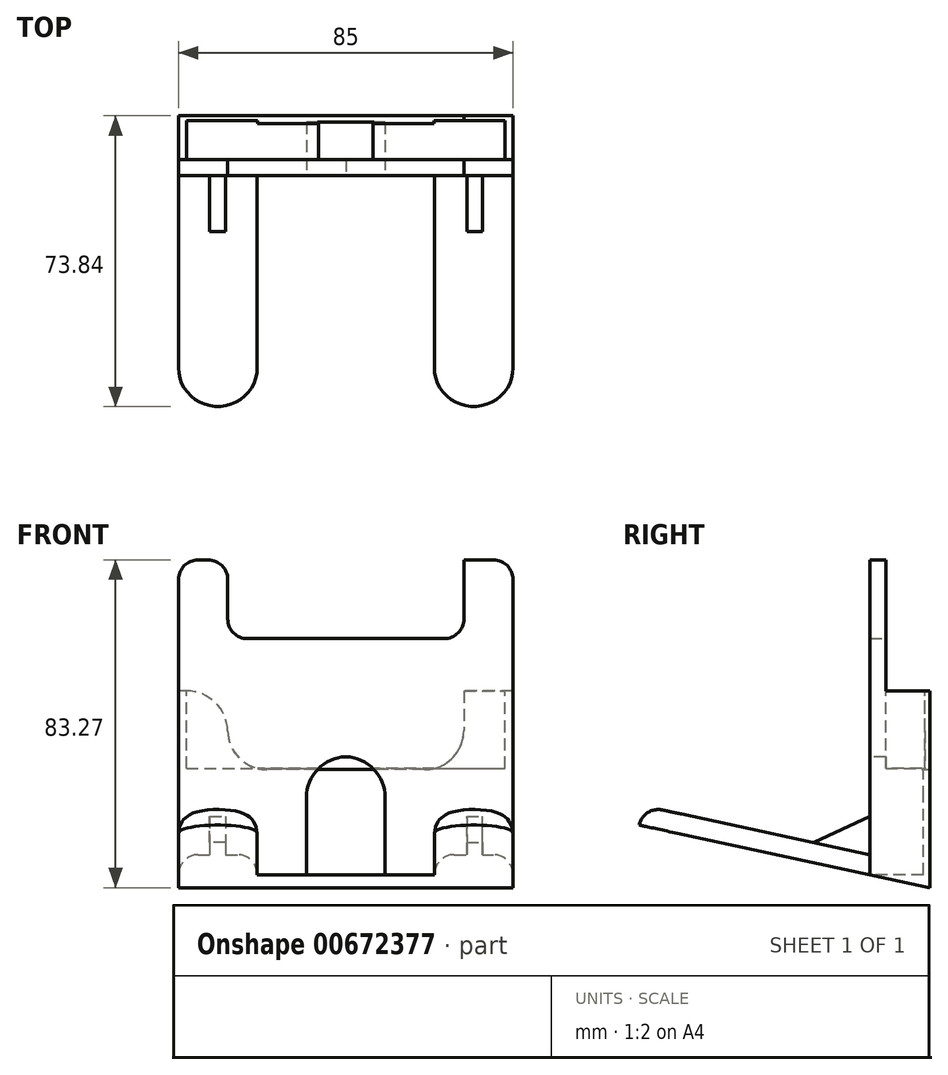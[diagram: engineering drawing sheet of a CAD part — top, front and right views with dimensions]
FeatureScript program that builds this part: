
annotation { "Feature Type Name" : "Feature", "Feature Type Description" : "" }
export const myFeature = defineFeature(function(context is Context, id is Id, definition is map)
    precondition{}
    {
        {
            var Q0;
            Q0=qCreatedBy(makeId("Right.planeOp"),FACE);
            var sketch = newSketch(context, id + "F0", { "sketchPlane" : qUnion([Q0])});
            skLineSegment(sketch, "E0", {"start": v(-12.15, -16.73) * mm, "end": v(-12.15, 63.27) * mm});
            skLineSegment(sketch, "E1", {"start": v(-12.15, 63.27) * mm, "end": v(-8.12, 63.27) * mm});
            skLineSegment(sketch, "E2", {"start": v(-8.12, 63.27) * mm, "end": v(-8.12, 30) * mm});
            skLineSegment(sketch, "E3", {"start": v(-8.12, 30) * mm, "end": v(3.04, 30) * mm});
            skLineSegment(sketch, "E4", {"start": v(3.04, 30) * mm, "end": v(3.04, -20) * mm});
            skLineSegment(sketch, "E5", {"start": v(3.04, -20) * mm, "end": v(-12.15, -16.73) * mm});
            skSolve(sketch);
        }
        {
            var Q0;
            Q0=makeQuery(id+"F0.imprint","IMPRINT",FACE,{"disambiguationData":[TD([[makeQuery(id+"F0.imprint","IMPRINT",EDGE,{"derivedFrom":sQuery(id+"F0.wireOp",EDGE,"E0")}),-1.0]])]});
            extrude(context, id + "F1", {"entities" : qUnion([Q0]), "depth" : 85 * mm, "offsetDistance" : 25 * mm});
        }
        {
            var Q0;
            Q0=makeQuery(id+"F1.opExtrude","SWEPT_FACE",FACE,{"disambiguationData":[OSD([sQuery(id+"F0.wireOp",EDGE,"E3")])]});
            cPlane(context, id + "F2", {"entities" : qUnion([Q0]), "cplaneType" : CPlaneType.OFFSET, "offset" : 0.3 * mm, "width" : 150 * mm, "height" : 150 * mm});
        }
        {
            var Q0;
            Q0=qCreatedBy(id+"F2.planeOp",FACE);
            var sketch = newSketch(context, id + "F3", { "sketchPlane" : qUnion([Q0])});
            skLineSegment(sketch, "E6.bottom", {"start": v(2, -8.12) * mm, "end": v(83, -8.12) * mm});
            skLineSegment(sketch, "E6.top", {"start": v(2, 1.88) * mm, "end": v(83, 1.88) * mm});
            skLineSegment(sketch, "E6.left", {"start": v(2, -8.12) * mm, "end": v(2, 1.88) * mm});
            skLineSegment(sketch, "E6.right", {"start": v(83, -8.12) * mm, "end": v(83, 1.88) * mm});
            skLineSegment(sketch, "E7", {"start": v(42.5, -18.88) * mm, "end": v(42.5, 22.7) * mm, "construction": true});
            skSolve(sketch);
        }
        {
            var Q0;
            Q0=makeQuery(id+"F3.imprint","IMPRINT",FACE,{"disambiguationData":[TD([[makeQuery(id+"F3.imprint","IMPRINT",EDGE,{"derivedFrom":sQuery(id+"F3.wireOp",EDGE,"E6.bottom")}),1.0]])]});
            extrude(context, id + "F4", {"entities" : qUnion([Q0]), "operationType" : NewBodyOperationType.REMOVE, "oppositeDirection" : true, "depth" : 20 * mm, "offsetDistance" : 25 * mm});
        }
        {
            var Q0;
            Q0=makeQuery(id+"F1.opExtrude","SWEPT_FACE",FACE,{"disambiguationData":[OSD([sQuery(id+"F0.wireOp",EDGE,"E0")])]});
            cPlane(context, id + "F5", {"entities" : qUnion([Q0]), "cplaneType" : CPlaneType.OFFSET, "offset" : 0 * mm, "width" : 150 * mm, "height" : 150 * mm});
        }
        {
            var Q0;
            Q0=qCreatedBy(id+"F5.planeOp",FACE);
            var sketch = newSketch(context, id + "F6", { "sketchPlane" : qUnion([Q0])});
            skLineSegment(sketch, "E8", {"start": v(42.5, 43.43) * mm, "end": v(42.5, -21.37) * mm, "construction": true});
            skLineSegment(sketch, "E9", {"start": v(42.5, -16.73) * mm, "end": v(32.5, -16.73) * mm});
            skLineSegment(sketch, "E10", {"start": v(32.5, -16.73) * mm, "end": v(32.5, 13.27) * mm});
            skLineSegment(sketch, "E11", {"start": v(32.5, 13.27) * mm, "end": v(42.5, 13.27) * mm});
            skLineSegment(sketch, "E12.MirrorCS", {"start": v(52.5, -16.73) * mm, "end": v(52.5, 13.27) * mm});
            skLineSegment(sketch, "E13.MirrorCS", {"start": v(42.5, -16.73) * mm, "end": v(52.5, -16.73) * mm});
            skLineSegment(sketch, "E14.MirrorCS", {"start": v(52.5, 13.27) * mm, "end": v(42.5, 13.27) * mm});
            skSolve(sketch);
        }
        {
            var Q0;
            Q0=makeQuery(id+"F6.imprint","IMPRINT",FACE,{"disambiguationData":[TD([[makeQuery(id+"F6.imprint","IMPRINT",EDGE,{"derivedFrom":sQuery(id+"F6.wireOp",EDGE,"E9")}),-1.0]])]});
            extrude(context, id + "F7", {"entities" : qUnion([Q0]), "operationType" : NewBodyOperationType.REMOVE, "oppositeDirection" : true, "depth" : 13.6 * mm, "offsetDistance" : 25 * mm});
        }
        {
            var Q0;
            Q0=makeQuery(id+"F1.opExtrude","SWEPT_FACE",FACE,{"disambiguationData":[OSD([sQuery(id+"F0.wireOp",EDGE,"E4")])]});
            cPlane(context, id + "F8", {"entities" : qUnion([Q0]), "cplaneType" : CPlaneType.OFFSET, "offset" : 0 * mm, "width" : 150 * mm, "height" : 150 * mm});
        }
        {
            var Q0;
            Q0=qCreatedBy(id+"F8.planeOp",FACE);
            var sketch = newSketch(context, id + "F9", { "sketchPlane" : qUnion([Q0])});
            skLineSegment(sketch, "E15.bottom", {"start": v(-72.5, 30) * mm, "end": v(-12.5, 30) * mm});
            skLineSegment(sketch, "E15.top", {"start": v(-72.5, 10) * mm, "end": v(-12.5, 10) * mm});
            skLineSegment(sketch, "E15.left", {"start": v(-72.5, 30) * mm, "end": v(-72.5, 10) * mm});
            skLineSegment(sketch, "E15.right", {"start": v(-12.5, 30) * mm, "end": v(-12.5, 10) * mm});
            skLineSegment(sketch, "E16", {"start": v(-42.5, 48.83) * mm, "end": v(-42.5, -16.28) * mm, "construction": true});
            skSolve(sketch);
        }
        {
            var Q0;
            Q0=makeQuery(id+"F9.imprint","IMPRINT",FACE,{"disambiguationData":[TD([[makeQuery(id+"F9.imprint","IMPRINT",EDGE,{"derivedFrom":sQuery(id+"F9.wireOp",EDGE,"E15.bottom")}),-1.0]])]});
            extrude(context, id + "F10", {"entities" : qUnion([Q0]), "operationType" : NewBodyOperationType.REMOVE, "oppositeDirection" : true, "depth" : 2 * mm, "offsetDistance" : 25 * mm});
        }
        {
            var Q0;
            Q0=makeQuery(id+"F1.opExtrude","SWEPT_FACE",FACE,{"disambiguationData":[OSD([sQuery(id+"F0.wireOp",EDGE,"E5")])]});
            cPlane(context, id + "F11", {"entities" : qUnion([Q0]), "cplaneType" : CPlaneType.OFFSET, "offset" : 0 * mm, "width" : 150 * mm, "height" : 150 * mm});
        }
        {
            var Q0;
            Q0=qCreatedBy(id+"F11.planeOp",FACE);
            var sketch = newSketch(context, id + "F12", { "sketchPlane" : qUnion([Q0])});
            skLineSegment(sketch, "E17.bottom", {"start": v(0, 8.35) * mm, "end": v(20, 8.35) * mm});
            skLineSegment(sketch, "E17.top", {"start": v(0, 68.35) * mm, "end": v(20, 68.35) * mm});
            skLineSegment(sketch, "E17.left", {"start": v(0, 8.35) * mm, "end": v(0, 68.35) * mm});
            skLineSegment(sketch, "E17.right", {"start": v(20, 8.35) * mm, "end": v(20, 68.35) * mm});
            skLineSegment(sketch, "E18", {"start": v(42.5, -22.48) * mm, "end": v(42.5, 41.37) * mm, "construction": true});
            skLineSegment(sketch, "E19.MirrorCS", {"start": v(65, 8.35) * mm, "end": v(65, 68.35) * mm});
            skLineSegment(sketch, "E20.MirrorCS", {"start": v(85, 68.35) * mm, "end": v(65, 68.35) * mm});
            skLineSegment(sketch, "E21.MirrorCS", {"start": v(85, 8.35) * mm, "end": v(85, 68.35) * mm});
            skLineSegment(sketch, "E22.MirrorCS", {"start": v(85, 8.35) * mm, "end": v(65, 8.35) * mm});
            skSolve(sketch);
        }
        {
            var Q0;
            Q0=makeQuery(id+"F12.imprint","IMPRINT",FACE,{"disambiguationData":[TD([[makeQuery(id+"F12.imprint","IMPRINT",EDGE,{"derivedFrom":sQuery(id+"F12.wireOp",EDGE,"E19.MirrorCS")}),-1.0]])]});
            var Q1;
            Q1=makeQuery(id+"F12.imprint","IMPRINT",FACE,{"disambiguationData":[TD([[makeQuery(id+"F12.imprint","IMPRINT",EDGE,{"derivedFrom":sQuery(id+"F12.wireOp",EDGE,"E17.bottom")}),1.0]])]});
            extrude(context, id + "F13", {"entities" : qUnion([Q0, Q1]), "operationType" : NewBodyOperationType.ADD, "oppositeDirection" : true, "depth" : 5 * mm, "offsetDistance" : 25 * mm});
        }
        {
            var Q0;
            Q0=makeQuery(id+"F13.opExtrude","SWEPT_EDGE",EDGE,{"disambiguationData":[OSD([sQuery(id+"F12.wireOp",EDGE,"E19.MirrorCS"),sQuery(id+"F12.wireOp",EDGE,"E20.MirrorCS")])]});
            var Q1;
            Q1=makeQuery(id+"F13.opExtrude","SWEPT_EDGE",EDGE,{"disambiguationData":[OSD([sQuery(id+"F12.wireOp",EDGE,"E17.top"),sQuery(id+"F12.wireOp",EDGE,"E17.left")])]});
            var Q2;
            Q2=makeQuery(id+"F13.opExtrude","SWEPT_EDGE",EDGE,{"disambiguationData":[OSD([sQuery(id+"F12.wireOp",EDGE,"E17.top"),sQuery(id+"F12.wireOp",EDGE,"E17.right")])]});
            var Q3;
            Q3=makeQuery(id+"F13.opExtrude","SWEPT_EDGE",EDGE,{"disambiguationData":[OSD([sQuery(id+"F12.wireOp",EDGE,"E20.MirrorCS"),sQuery(id+"F12.wireOp",EDGE,"E21.MirrorCS")])]});
            fillet(context, id + "F14", {"entities" : qUnion([Q0, Q1, Q2, Q3]), "radius" : 10 * mm, "tangentPropagation" : true, "allowEdgeOverflow" : false});
        }
        {
            var Q0;
            Q0=makeQuery(id+"F13.opExtrude","CAP_EDGE",EDGE,{"disambiguationData":[OSD([sQuery(id+"F12.wireOp",EDGE,"E21.MirrorCS")])],"isStart":false});
            var Q1;
            Q1=makeQuery(id+"F13.opExtrude","CAP_EDGE",EDGE,{"disambiguationData":[OSD([sQuery(id+"F12.wireOp",EDGE,"E17.right")])],"isStart":false});
            fillet(context, id + "F15", {"entities" : qUnion([Q0, Q1]), "radius" : 5 * mm, "tangentPropagation" : true, "allowEdgeOverflow" : false});
        }
        {
            var Q0;
            Q0=makeQuery(id+"F10.boolean.opBoolean","COPY",EDGE,{"derivedFrom":makeQuery(id+"F10.opExtrude","SWEPT_EDGE",EDGE,{"disambiguationData":[OSD([sQuery(id+"F9.wireOp",EDGE,"E15.top"),sQuery(id+"F9.wireOp",EDGE,"E15.right")])]})});
            var Q1;
            Q1=makeQuery(id+"F10.boolean.opBoolean","COPY",EDGE,{"derivedFrom":makeQuery(id+"F10.opExtrude","SWEPT_EDGE",EDGE,{"disambiguationData":[OSD([sQuery(id+"F9.wireOp",EDGE,"E15.top"),sQuery(id+"F9.wireOp",EDGE,"E15.left")])]})});
            fillet(context, id + "F16", {"entities" : qUnion([Q0, Q1]), "radius" : 10 * mm, "tangentPropagation" : true, "allowEdgeOverflow" : false});
        }
        {
            var Q0;
            Q0=makeQuery(id+"F4.boolean.opBoolean","MERGE",FACE,{"derivedFrom":[makeQuery(id+"F1.opExtrude","SWEPT_FACE",FACE,{"disambiguationData":[OSD([sQuery(id+"F0.wireOp",EDGE,"E2")])]}),makeQuery(id+"F4.opExtrude","SWEPT_FACE",FACE,{"disambiguationData":[OSD([sQuery(id+"F3.wireOp",EDGE,"E6.bottom")])]})]});
            cPlane(context, id + "F17", {"entities" : qUnion([Q0]), "cplaneType" : CPlaneType.OFFSET, "offset" : 0 * mm, "width" : 150 * mm, "height" : 150 * mm});
        }
        {
            var Q0;
            Q0=qCreatedBy(id+"F17.planeOp",FACE);
            var sketch = newSketch(context, id + "F18", { "sketchPlane" : qUnion([Q0])});
            skLineSegment(sketch, "E23.bottom", {"start": v(-72.5, 63.27) * mm, "end": v(-12.5, 63.27) * mm});
            skLineSegment(sketch, "E23.top", {"start": v(-72.5, 43.27) * mm, "end": v(-12.5, 43.27) * mm});
            skLineSegment(sketch, "E23.left", {"start": v(-72.5, 63.27) * mm, "end": v(-72.5, 43.27) * mm});
            skLineSegment(sketch, "E23.right", {"start": v(-12.5, 63.27) * mm, "end": v(-12.5, 43.27) * mm});
            skLineSegment(sketch, "E24", {"start": v(-42.5, 59.86) * mm, "end": v(-42.5, -10.53) * mm, "construction": true});
            skSolve(sketch);
        }
        {
            var Q0;
            Q0=makeQuery(id+"F18.imprint","IMPRINT",FACE,{"disambiguationData":[TD([[makeQuery(id+"F18.imprint","IMPRINT",EDGE,{"derivedFrom":sQuery(id+"F18.wireOp",EDGE,"E23.bottom")}),-1.0]])]});
            extrude(context, id + "F19", {"entities" : qUnion([Q0]), "operationType" : NewBodyOperationType.REMOVE, "oppositeDirection" : true, "depth" : 4.5 * mm, "offsetDistance" : 25 * mm});
        }
        {
            var Q0;
            Q0=makeQuery(id+"F19.boolean.opBoolean","COPY",EDGE,{"derivedFrom":makeQuery(id+"F19.opExtrude","SWEPT_EDGE",EDGE,{"disambiguationData":[OSD([sQuery(id+"F18.wireOp",EDGE,"E23.bottom"),sQuery(id+"F18.wireOp",EDGE,"E23.left")])]})});
            var Q1;
            Q1=makeQuery(id+"F1.opExtrude","CAP_EDGE",EDGE,{"disambiguationData":[OSD([sQuery(id+"F0.wireOp",EDGE,"E1")])],"isStart":false});
            var Q2;
            Q2=makeQuery(id+"F19.boolean.opBoolean","COPY",EDGE,{"derivedFrom":makeQuery(id+"F19.opExtrude","SWEPT_EDGE",EDGE,{"disambiguationData":[OSD([sQuery(id+"F18.wireOp",EDGE,"E23.top"),sQuery(id+"F18.wireOp",EDGE,"E23.left")])]})});
            var Q3;
            Q3=makeQuery(id+"F19.boolean.opBoolean","COPY",EDGE,{"derivedFrom":makeQuery(id+"F19.opExtrude","SWEPT_EDGE",EDGE,{"disambiguationData":[OSD([sQuery(id+"F18.wireOp",EDGE,"E23.top"),sQuery(id+"F18.wireOp",EDGE,"E23.right")])]})});
            var Q4;
            Q4=makeQuery(id+"F19.boolean.opBoolean","COPY",EDGE,{"derivedFrom":makeQuery(id+"F19.opExtrude","SWEPT_EDGE",EDGE,{"disambiguationData":[OSD([sQuery(id+"F18.wireOp",EDGE,"E23.bottom"),sQuery(id+"F18.wireOp",EDGE,"E23.right")])]})});
            var Q5;
            Q5=makeQuery(id+"F1.opExtrude","CAP_EDGE",EDGE,{"disambiguationData":[OSD([sQuery(id+"F0.wireOp",EDGE,"E1")])],"isStart":true});
            fillet(context, id + "F20", {"entities" : qUnion([Q0, Q1, Q2, Q3, Q4, Q5]), "radius" : 5 * mm, "tangentPropagation" : true, "allowEdgeOverflow" : false});
        }
        {
            var Q0;
            Q0=makeQuery(id+"F10.boolean.opBoolean","COPY",EDGE,{"derivedFrom":makeQuery(id+"F10.opExtrude","SWEPT_EDGE",EDGE,{"disambiguationData":[OSD([sQuery(id+"F9.wireOp",EDGE,"E15.bottom"),sQuery(id+"F9.wireOp",EDGE,"E15.left")])]})});
            var Q1;
            Q1=makeQuery(id+"F10.boolean.opBoolean","COPY",EDGE,{"derivedFrom":makeQuery(id+"F10.opExtrude","SWEPT_EDGE",EDGE,{"disambiguationData":[OSD([sQuery(id+"F9.wireOp",EDGE,"E15.bottom"),sQuery(id+"F9.wireOp",EDGE,"E15.right")])]})});
            fillet(context, id + "F21", {"entities" : qUnion([Q0, Q1]), "radius" : 10.45 * mm, "tangentPropagation" : true, "allowEdgeOverflow" : false});
        }
        {
            var Q0;
            Q0=qCreatedBy(id+"F17.planeOp",FACE);
            var sketch = newSketch(context, id + "F22", { "sketchPlane" : qUnion([Q0])});
            skLineSegment(sketch, "E25.bottom", {"start": v(-7.94, -13) * mm, "end": v(-11.94, -13) * mm});
            skLineSegment(sketch, "E25.top", {"start": v(-7.94, 0) * mm, "end": v(-11.94, 0) * mm});
            skLineSegment(sketch, "E25.left", {"start": v(-7.94, -13) * mm, "end": v(-7.94, 0) * mm});
            skLineSegment(sketch, "E25.right", {"start": v(-11.94, -13) * mm, "end": v(-11.94, 0) * mm});
            skSolve(sketch);
        }
        {
            var Q0;
            Q0 = qSketchRegion(id + "F22", true);
            extrude(context, id + "F23", {"entities" : qUnion([Q0]), "operationType" : NewBodyOperationType.ADD, "oppositeDirection" : true, "depth" : 20 * mm, "offsetDistance" : 25 * mm});
        }
        {
            var Q0;
            Q0=makeQuery(id+"F23.opExtrude","CAP_EDGE",EDGE,{"disambiguationData":[OSD([sQuery(id+"F22.wireOp",EDGE,"E25.top")])],"isStart":false});
            chamfer(context, id + "F24", {"entities" : qUnion([Q0]), "chamferType" : ChamferType.OFFSET_ANGLE, "width" : 20 * mm, "oppositeDirection" : false, "angle" : 25 * degree, "tangentPropagation" : true});
        }
        {
            var Q0;
            Q0=makeQuery(id+"F1.opExtrude","SWEPT_FACE",FACE,{"disambiguationData":[OSD([sQuery(id+"F0.wireOp",EDGE,"E0")])]});
            var sketch = newSketch(context, id + "F25", { "sketchPlane" : qUnion([Q0])});
            skLineSegment(sketch, "E26.bottom", {"start": v(73.25, -11.61) * mm, "end": v(77.25, -11.61) * mm});
            skLineSegment(sketch, "E26.top", {"start": v(73.25, -1.88) * mm, "end": v(77.25, -1.88) * mm});
            skLineSegment(sketch, "E26.left", {"start": v(73.25, -11.61) * mm, "end": v(73.25, -1.88) * mm});
            skLineSegment(sketch, "E26.right", {"start": v(77.25, -11.61) * mm, "end": v(77.25, -1.88) * mm});
            skSolve(sketch);
        }
        {
            var Q0;
            Q0=makeQuery(id+"F25.imprint","IMPRINT",FACE,{"disambiguationData":[TD([[makeQuery(id+"F25.imprint","IMPRINT",EDGE,{"derivedFrom":sQuery(id+"F25.wireOp",EDGE,"E26.bottom")}),1.0]])]});
            extrude(context, id + "F26", {"entities" : qUnion([Q0]), "operationType" : NewBodyOperationType.ADD, "depth" : 15 * mm, "offsetDistance" : 25 * mm});
        }
        {
            var Q0;
            Q0=makeQuery(id+"F26.opExtrude","CAP_EDGE",EDGE,{"disambiguationData":[OSD([sQuery(id+"F25.wireOp",EDGE,"E26.top")])],"isStart":false});
            chamfer(context, id + "F27", {"entities" : qUnion([Q0]), "chamferType" : ChamferType.OFFSET_ANGLE, "width" : 15 * mm, "oppositeDirection" : false, "angle" : 25 * degree, "tangentPropagation" : true});
        }
        {
            var Q0;
            Q0=makeQuery(id+"F7.boolean.opBoolean","COPY",EDGE,{"derivedFrom":makeQuery(id+"F7.opExtrude","SWEPT_EDGE",EDGE,{"disambiguationData":[OSD([sQuery(id+"F6.wireOp",EDGE,"E10"),sQuery(id+"F6.wireOp",EDGE,"E11")])]})});
            var Q1;
            Q1=makeQuery(id+"F7.boolean.opBoolean","COPY",EDGE,{"derivedFrom":makeQuery(id+"F7.opExtrude","SWEPT_EDGE",EDGE,{"disambiguationData":[OSD([sQuery(id+"F6.wireOp",EDGE,"E12.MirrorCS"),sQuery(id+"F6.wireOp",EDGE,"E14.MirrorCS")])]})});
            fillet(context, id + "F28", {"entities" : qUnion([Q0, Q1]), "radius" : 10.38 * mm, "tangentPropagation" : true, "allowEdgeOverflow" : false});
        }
    });
